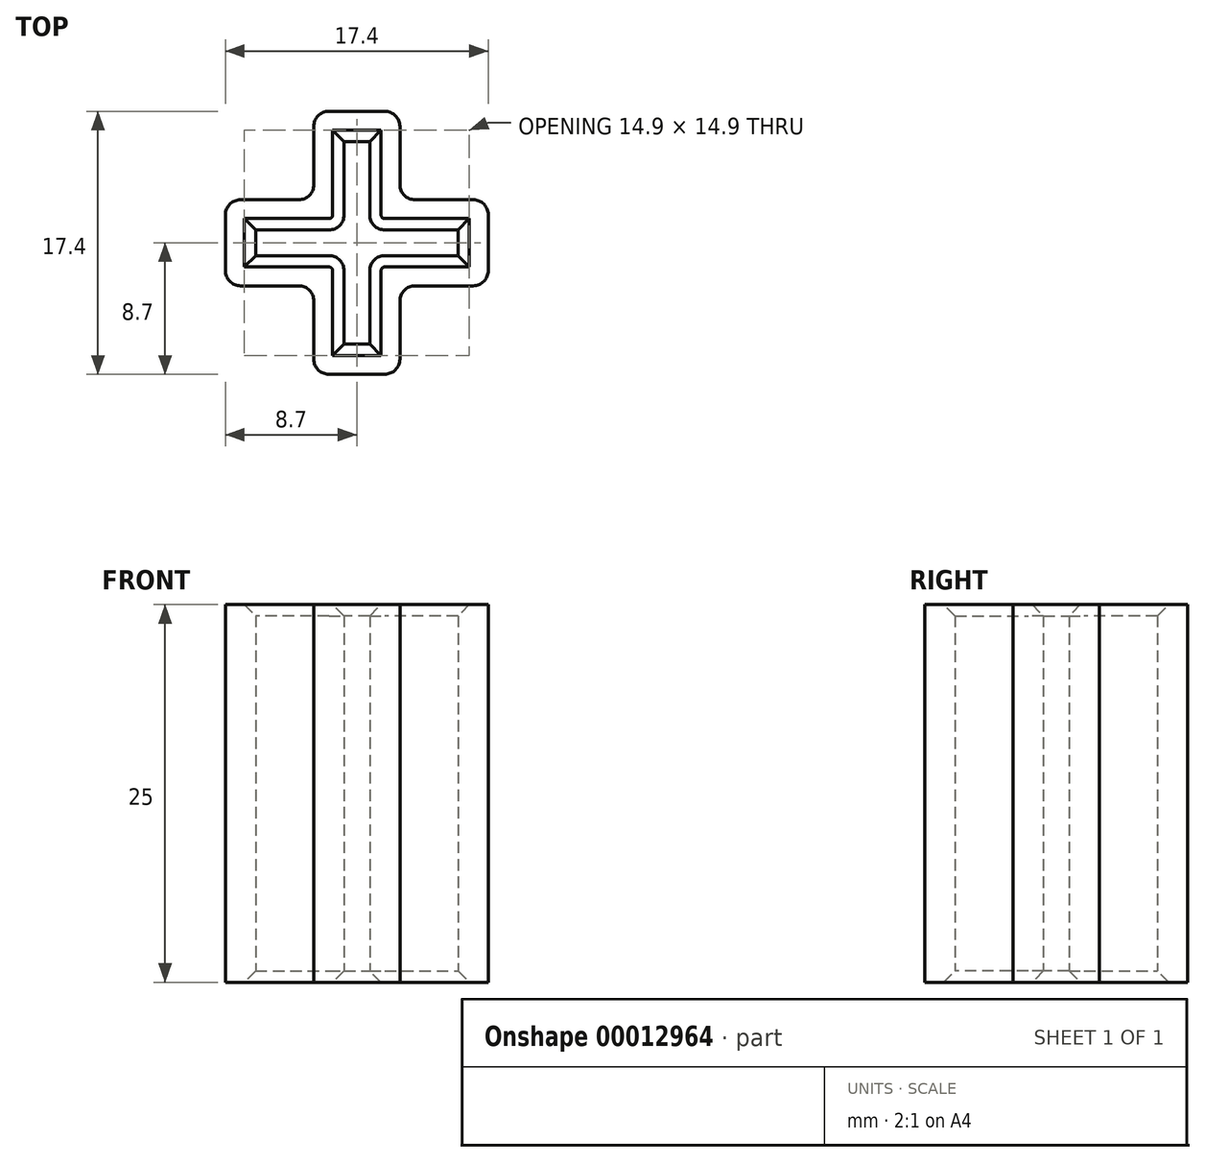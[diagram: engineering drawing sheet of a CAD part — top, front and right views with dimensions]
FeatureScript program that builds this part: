
annotation { "Feature Type Name" : "Feature", "Feature Type Description" : "" }
export const myFeature = defineFeature(function(context is Context, id is Id, definition is map)
    precondition{}
    {
        {
            var Q0;
            Q0=qCreatedBy(makeId("Top.planeOp"),FACE);
            var sketch = newSketch(context, id + "F0", { "sketchPlane" : qUnion([Q0])});
            skLineSegment(sketch, "E0.rect.bottom", {"start": v(-0.85, 6.7) * mm, "end": v(0.85, 6.7) * mm});
            skLineSegment(sketch, "E0.rect.top", {"start": v(-0.85, -6.7) * mm, "end": v(0.85, -6.7) * mm});
            skLineSegment(sketch, "E0.rect.left", {"start": v(-0.85, 6.7) * mm, "end": v(-0.85, -6.7) * mm});
            skLineSegment(sketch, "E0.rect.right", {"start": v(0.85, 6.7) * mm, "end": v(0.85, -6.7) * mm});
            skPoint(sketch, "E0.rect.middle", {"position": v(0, 0) * mm});
            skLineSegment(sketch, "E1.rect.bottom", {"start": v(-6.7, 0.85) * mm, "end": v(6.7, 0.85) * mm});
            skLineSegment(sketch, "E1.rect.top", {"start": v(-6.7, -0.85) * mm, "end": v(6.7, -0.85) * mm});
            skLineSegment(sketch, "E1.rect.left", {"start": v(-6.7, 0.85) * mm, "end": v(-6.7, -0.85) * mm});
            skLineSegment(sketch, "E1.rect.right", {"start": v(6.7, 0.85) * mm, "end": v(6.7, -0.85) * mm});
            skLineSegment(sketch, "E2.0", {"start": v(-8.7, 2.85) * mm, "end": v(8.7, 2.85) * mm});
            skLineSegment(sketch, "E2.1", {"start": v(-8.7, 2.85) * mm, "end": v(-8.7, -2.85) * mm});
            skLineSegment(sketch, "E2.2", {"start": v(-8.7, -2.85) * mm, "end": v(8.7, -2.85) * mm});
            skLineSegment(sketch, "E2.3", {"start": v(8.7, 2.85) * mm, "end": v(8.7, -2.85) * mm});
            skLineSegment(sketch, "E3.0", {"start": v(-2.85, 8.7) * mm, "end": v(-2.85, -8.7) * mm});
            skLineSegment(sketch, "E3.1", {"start": v(-2.85, 8.7) * mm, "end": v(2.85, 8.7) * mm});
            skLineSegment(sketch, "E3.2", {"start": v(2.85, 8.7) * mm, "end": v(2.85, -8.7) * mm});
            skLineSegment(sketch, "E3.3", {"start": v(-2.85, -8.7) * mm, "end": v(2.85, -8.7) * mm});
            skSolve(sketch);
        }
        {
            var Q0;
            {var subQ10=sQuery(id+"F0.wireOp",EDGE,"E1.rect.left");Q0=makeQuery(id+"F0.imprint","IMPRINT",FACE,{"disambiguationData":[TD([[makeQuery(id+"F0.imprint","IMPRINT",EDGE,{"derivedFrom":subQ10}),-1.0]])]});}
            var Q1;
            {var subQ1=sQuery(id+"F0.wireOp",EDGE,"E0.rect.left");var subQ5=sQuery(id+"F0.wireOp",EDGE,"E1.rect.top");var subQ7=makeQuery(id+"F0.imprint","INTERSECT",VERTEX,{"derivedFrom":[subQ1,subQ5]});Q1=makeQuery(id+"F0.imprint","IMPRINT",FACE,{"disambiguationData":[TD([[makeQuery(id+"F0.imprint","IMPRINT",EDGE,{"disambiguationData":[TD([[subQ7,-1.0]])],"derivedFrom":subQ1}),-1.0]])]});}
            var Q2;
            {var subQ10=sQuery(id+"F0.wireOp",EDGE,"E0.rect.top");Q2=makeQuery(id+"F0.imprint","IMPRINT",FACE,{"disambiguationData":[TD([[makeQuery(id+"F0.imprint","IMPRINT",EDGE,{"derivedFrom":subQ10}),-1.0]])]});}
            var Q3;
            {var subQ3=sQuery(id+"F0.wireOp",EDGE,"E2.0");var subQ5=sQuery(id+"F0.wireOp",EDGE,"E0.rect.left");var subQ6=makeQuery(id+"F0.imprint","INTERSECT",VERTEX,{"derivedFrom":[subQ5,subQ3]});Q3=makeQuery(id+"F0.imprint","IMPRINT",FACE,{"disambiguationData":[TD([[makeQuery(id+"F0.imprint","IMPRINT",EDGE,{"disambiguationData":[TD([[subQ6,-1.0]])],"derivedFrom":subQ5}),-1.0]])]});}
            var Q4;
            {var subQ10=sQuery(id+"F0.wireOp",EDGE,"E0.rect.bottom");Q4=makeQuery(id+"F0.imprint","IMPRINT",FACE,{"disambiguationData":[TD([[makeQuery(id+"F0.imprint","IMPRINT",EDGE,{"derivedFrom":subQ10}),1.0]])]});}
            var Q5;
            {var subQ3=sQuery(id+"F0.wireOp",EDGE,"E2.0");var subQ5=sQuery(id+"F0.wireOp",EDGE,"E0.rect.right");var subQ6=makeQuery(id+"F0.imprint","INTERSECT",VERTEX,{"derivedFrom":[subQ5,subQ3]});Q5=makeQuery(id+"F0.imprint","IMPRINT",FACE,{"disambiguationData":[TD([[makeQuery(id+"F0.imprint","IMPRINT",EDGE,{"disambiguationData":[TD([[subQ6,-1.0]])],"derivedFrom":subQ5}),1.0]])]});}
            var Q6;
            {var subQ1=sQuery(id+"F0.wireOp",EDGE,"E1.rect.top");var subQ5=sQuery(id+"F0.wireOp",EDGE,"E0.rect.right");var subQ7=makeQuery(id+"F0.imprint","INTERSECT",VERTEX,{"derivedFrom":[subQ5,subQ1]});Q6=makeQuery(id+"F0.imprint","IMPRINT",FACE,{"disambiguationData":[TD([[makeQuery(id+"F0.imprint","IMPRINT",EDGE,{"disambiguationData":[TD([[subQ7,-1.0]])],"derivedFrom":subQ5}),1.0]])]});}
            var Q7;
            {var subQ10=sQuery(id+"F0.wireOp",EDGE,"E1.rect.right");Q7=makeQuery(id+"F0.imprint","IMPRINT",FACE,{"disambiguationData":[TD([[makeQuery(id+"F0.imprint","IMPRINT",EDGE,{"derivedFrom":subQ10}),1.0]])]});}
            extrude(context, id + "F1", {"entities" : qUnion([Q0, Q1, Q2, Q3, Q4, Q5, Q6, Q7]), "endBound" : BoundingType.SYMMETRIC, "depth" : 25 * mm});
        }
        {
            var Q0;
            Q0=makeQuery(id+"F1.opExtrude","SWEPT_EDGE",EDGE,{"disambiguationData":[OSD([sQuery(id+"F0.wireOp",EDGE,"E0.rect.left"),sQuery(id+"F0.wireOp",EDGE,"E1.rect.top")])]});
            var Q1;
            Q1=makeQuery(id+"F1.opExtrude","SWEPT_EDGE",EDGE,{"disambiguationData":[OSD([sQuery(id+"F0.wireOp",EDGE,"E0.rect.right"),sQuery(id+"F0.wireOp",EDGE,"E1.rect.top")])]});
            var Q2;
            Q2=makeQuery(id+"F1.opExtrude","SWEPT_EDGE",EDGE,{"disambiguationData":[OSD([sQuery(id+"F0.wireOp",EDGE,"E0.rect.right"),sQuery(id+"F0.wireOp",EDGE,"E1.rect.bottom")])]});
            var Q3;
            Q3=makeQuery(id+"F1.opExtrude","SWEPT_EDGE",EDGE,{"disambiguationData":[OSD([sQuery(id+"F0.wireOp",EDGE,"E0.rect.left"),sQuery(id+"F0.wireOp",EDGE,"E1.rect.bottom")])]});
            fillet(context, id + "F2", {"entities" : qUnion([Q0, Q1, Q2, Q3]), "radius" : 1 * mm, "tangentPropagation" : true, "allowEdgeOverflow" : false});
        }
        {
            var Q0;
            Q0=makeQuery(id+"F1.opExtrude","SWEPT_EDGE",EDGE,{"disambiguationData":[OSD([sQuery(id+"F0.wireOp",EDGE,"E2.0"),sQuery(id+"F0.wireOp",EDGE,"E3.0")])]});
            var Q1;
            Q1=makeQuery(id+"F1.opExtrude","SWEPT_EDGE",EDGE,{"disambiguationData":[OSD([sQuery(id+"F0.wireOp",EDGE,"E2.0"),sQuery(id+"F0.wireOp",EDGE,"E2.1")])]});
            var Q2;
            Q2=makeQuery(id+"F1.opExtrude","SWEPT_EDGE",EDGE,{"disambiguationData":[OSD([sQuery(id+"F0.wireOp",EDGE,"E2.1"),sQuery(id+"F0.wireOp",EDGE,"E2.2")])]});
            var Q3;
            Q3=makeQuery(id+"F1.opExtrude","SWEPT_EDGE",EDGE,{"disambiguationData":[OSD([sQuery(id+"F0.wireOp",EDGE,"E3.0"),sQuery(id+"F0.wireOp",EDGE,"E3.1")])]});
            var Q4;
            Q4=makeQuery(id+"F1.opExtrude","SWEPT_EDGE",EDGE,{"disambiguationData":[OSD([sQuery(id+"F0.wireOp",EDGE,"E3.1"),sQuery(id+"F0.wireOp",EDGE,"E3.2")])]});
            var Q5;
            Q5=makeQuery(id+"F1.opExtrude","SWEPT_EDGE",EDGE,{"disambiguationData":[OSD([sQuery(id+"F0.wireOp",EDGE,"E2.0"),sQuery(id+"F0.wireOp",EDGE,"E2.3")])]});
            var Q6;
            Q6=makeQuery(id+"F1.opExtrude","SWEPT_EDGE",EDGE,{"disambiguationData":[OSD([sQuery(id+"F0.wireOp",EDGE,"E3.0"),sQuery(id+"F0.wireOp",EDGE,"E3.3")])]});
            var Q7;
            Q7=makeQuery(id+"F1.opExtrude","SWEPT_EDGE",EDGE,{"disambiguationData":[OSD([sQuery(id+"F0.wireOp",EDGE,"E2.2"),sQuery(id+"F0.wireOp",EDGE,"E3.0")])]});
            var Q8;
            Q8=makeQuery(id+"F1.opExtrude","SWEPT_EDGE",EDGE,{"disambiguationData":[OSD([sQuery(id+"F0.wireOp",EDGE,"E3.2"),sQuery(id+"F0.wireOp",EDGE,"E3.3")])]});
            var Q9;
            Q9=makeQuery(id+"F1.opExtrude","SWEPT_EDGE",EDGE,{"disambiguationData":[OSD([sQuery(id+"F0.wireOp",EDGE,"E2.2"),sQuery(id+"F0.wireOp",EDGE,"E2.3")])]});
            var Q10;
            Q10=makeQuery(id+"F1.opExtrude","SWEPT_EDGE",EDGE,{"disambiguationData":[OSD([sQuery(id+"F0.wireOp",EDGE,"E2.2"),sQuery(id+"F0.wireOp",EDGE,"E3.2")])]});
            var Q11;
            Q11=makeQuery(id+"F1.opExtrude","SWEPT_EDGE",EDGE,{"disambiguationData":[OSD([sQuery(id+"F0.wireOp",EDGE,"E2.0"),sQuery(id+"F0.wireOp",EDGE,"E3.2")])]});
            fillet(context, id + "F3", {"entities" : qUnion([Q0, Q1, Q2, Q3, Q4, Q5, Q6, Q7, Q8, Q9, Q10, Q11]), "radius" : 1 * mm, "tangentPropagation" : true, "allowEdgeOverflow" : false});
        }
        {
            var Q0;
            {var subQ0=sQuery(id+"F0.wireOp",EDGE,"E1.rect.bottom");Q0=makeQuery(id+"F1.opExtrude","CAP_EDGE",EDGE,{"disambiguationData":[OSD([subQ0]),TDD([makeQuery(id+"F0.imprint","IMPRINT",EDGE,{"disambiguationData":[TD([[makeQuery(id+"F0.imprint","INTERSECT",VERTEX,{"derivedFrom":[subQ0,sQuery(id+"F0.wireOp",EDGE,"E1.rect.left")]}),-1.0]])],"derivedFrom":subQ0}),makeQuery(id+"F0.imprint","IMPRINT",EDGE,{"disambiguationData":[TD([[makeQuery(id+"F0.imprint","INTERSECT",VERTEX,{"derivedFrom":[sQuery(id+"F0.wireOp",EDGE,"E0.rect.left"),subQ0]}),1.0]])],"derivedFrom":subQ0})])],"isStart":false});}
            var Q1;
            {var subQ0=sQuery(id+"F0.wireOp",EDGE,"E0.rect.right");var subQ1=makeQuery(id+"F0.imprint","INTERSECT",VERTEX,{"derivedFrom":[subQ0,sQuery(id+"F0.wireOp",EDGE,"E2.0")]});Q1=makeQuery(id+"F1.opExtrude","CAP_EDGE",EDGE,{"disambiguationData":[OSD([subQ0]),TDD([makeQuery(id+"F0.imprint","IMPRINT",EDGE,{"disambiguationData":[TD([[makeQuery(id+"F0.imprint","INTERSECT",VERTEX,{"derivedFrom":[sQuery(id+"F0.wireOp",EDGE,"E0.rect.bottom"),subQ0]}),-1.0]])],"derivedFrom":subQ0}),makeQuery(id+"F0.imprint","IMPRINT",EDGE,{"disambiguationData":[TD([[subQ1,-1.0]])],"derivedFrom":subQ0})])],"isStart":false});}
            var Q2;
            {var subQ0=sQuery(id+"F0.wireOp",EDGE,"E1.rect.top");Q2=makeQuery(id+"F1.opExtrude","CAP_EDGE",EDGE,{"disambiguationData":[OSD([subQ0]),TDD([makeQuery(id+"F0.imprint","IMPRINT",EDGE,{"disambiguationData":[TD([[makeQuery(id+"F0.imprint","INTERSECT",VERTEX,{"derivedFrom":[sQuery(id+"F0.wireOp",EDGE,"E0.rect.right"),subQ0]}),-1.0]])],"derivedFrom":subQ0}),makeQuery(id+"F0.imprint","IMPRINT",EDGE,{"disambiguationData":[TD([[makeQuery(id+"F0.imprint","INTERSECT",VERTEX,{"derivedFrom":[subQ0,sQuery(id+"F0.wireOp",EDGE,"E1.rect.right")]}),1.0]])],"derivedFrom":subQ0})])],"isStart":false});}
            var Q3;
            {var subQ0=sQuery(id+"F0.wireOp",EDGE,"E0.rect.left");Q3=makeQuery(id+"F1.opExtrude","CAP_EDGE",EDGE,{"disambiguationData":[OSD([subQ0]),TDD([makeQuery(id+"F0.imprint","IMPRINT",EDGE,{"disambiguationData":[TD([[makeQuery(id+"F0.imprint","INTERSECT",VERTEX,{"derivedFrom":[subQ0,sQuery(id+"F0.wireOp",EDGE,"E1.rect.top")]}),-1.0]])],"derivedFrom":subQ0}),makeQuery(id+"F0.imprint","IMPRINT",EDGE,{"disambiguationData":[TD([[makeQuery(id+"F0.imprint","INTERSECT",VERTEX,{"derivedFrom":[sQuery(id+"F0.wireOp",EDGE,"E0.rect.top"),subQ0]}),1.0]])],"derivedFrom":subQ0})])],"isStart":false});}
            var Q4;
            Q4=makeQuery(id+"F1.opExtrude","CAP_EDGE",EDGE,{"disambiguationData":[OSD([sQuery(id+"F0.wireOp",EDGE,"E1.rect.left")])],"isStart":false});
            var Q5;
            Q5=makeQuery(id+"F1.opExtrude","CAP_EDGE",EDGE,{"disambiguationData":[OSD([sQuery(id+"F0.wireOp",EDGE,"E0.rect.bottom")])],"isStart":false});
            var Q6;
            Q6=makeQuery(id+"F1.opExtrude","CAP_EDGE",EDGE,{"disambiguationData":[OSD([sQuery(id+"F0.wireOp",EDGE,"E1.rect.right")])],"isStart":false});
            var Q7;
            Q7=makeQuery(id+"F1.opExtrude","CAP_EDGE",EDGE,{"disambiguationData":[OSD([sQuery(id+"F0.wireOp",EDGE,"E0.rect.top")])],"isStart":false});
            var Q8;
            {var subQ0=sQuery(id+"F0.wireOp",EDGE,"E0.rect.right");Q8=makeQuery(id+"F1.opExtrude","CAP_EDGE",EDGE,{"disambiguationData":[OSD([subQ0]),TDD([makeQuery(id+"F0.imprint","IMPRINT",EDGE,{"disambiguationData":[TD([[makeQuery(id+"F0.imprint","INTERSECT",VERTEX,{"derivedFrom":[subQ0,sQuery(id+"F0.wireOp",EDGE,"E1.rect.top")]}),-1.0]])],"derivedFrom":subQ0}),makeQuery(id+"F0.imprint","IMPRINT",EDGE,{"disambiguationData":[TD([[makeQuery(id+"F0.imprint","INTERSECT",VERTEX,{"derivedFrom":[sQuery(id+"F0.wireOp",EDGE,"E0.rect.top"),subQ0]}),1.0]])],"derivedFrom":subQ0})])],"isStart":true});}
            var Q9;
            {var subQ0=sQuery(id+"F0.wireOp",EDGE,"E0.rect.left");Q9=makeQuery(id+"F1.opExtrude","CAP_EDGE",EDGE,{"disambiguationData":[OSD([subQ0]),TDD([makeQuery(id+"F0.imprint","IMPRINT",EDGE,{"disambiguationData":[TD([[makeQuery(id+"F0.imprint","INTERSECT",VERTEX,{"derivedFrom":[subQ0,sQuery(id+"F0.wireOp",EDGE,"E1.rect.top")]}),-1.0]])],"derivedFrom":subQ0}),makeQuery(id+"F0.imprint","IMPRINT",EDGE,{"disambiguationData":[TD([[makeQuery(id+"F0.imprint","INTERSECT",VERTEX,{"derivedFrom":[sQuery(id+"F0.wireOp",EDGE,"E0.rect.top"),subQ0]}),1.0]])],"derivedFrom":subQ0})])],"isStart":true});}
            var Q10;
            {var subQ0=sQuery(id+"F0.wireOp",EDGE,"E1.rect.bottom");Q10=makeQuery(id+"F1.opExtrude","CAP_EDGE",EDGE,{"disambiguationData":[OSD([subQ0]),TDD([makeQuery(id+"F0.imprint","IMPRINT",EDGE,{"disambiguationData":[TD([[makeQuery(id+"F0.imprint","INTERSECT",VERTEX,{"derivedFrom":[subQ0,sQuery(id+"F0.wireOp",EDGE,"E1.rect.left")]}),-1.0]])],"derivedFrom":subQ0}),makeQuery(id+"F0.imprint","IMPRINT",EDGE,{"disambiguationData":[TD([[makeQuery(id+"F0.imprint","INTERSECT",VERTEX,{"derivedFrom":[sQuery(id+"F0.wireOp",EDGE,"E0.rect.left"),subQ0]}),1.0]])],"derivedFrom":subQ0})])],"isStart":true});}
            var Q11;
            {var subQ0=sQuery(id+"F0.wireOp",EDGE,"E0.rect.right");var subQ1=makeQuery(id+"F0.imprint","INTERSECT",VERTEX,{"derivedFrom":[subQ0,sQuery(id+"F0.wireOp",EDGE,"E2.0")]});Q11=makeQuery(id+"F1.opExtrude","CAP_EDGE",EDGE,{"disambiguationData":[OSD([subQ0]),TDD([makeQuery(id+"F0.imprint","IMPRINT",EDGE,{"disambiguationData":[TD([[makeQuery(id+"F0.imprint","INTERSECT",VERTEX,{"derivedFrom":[sQuery(id+"F0.wireOp",EDGE,"E0.rect.bottom"),subQ0]}),-1.0]])],"derivedFrom":subQ0}),makeQuery(id+"F0.imprint","IMPRINT",EDGE,{"disambiguationData":[TD([[subQ1,-1.0]])],"derivedFrom":subQ0})])],"isStart":true});}
            var Q12;
            Q12=makeQuery(id+"F1.opExtrude","CAP_EDGE",EDGE,{"disambiguationData":[OSD([sQuery(id+"F0.wireOp",EDGE,"E1.rect.right")])],"isStart":true});
            var Q13;
            Q13=makeQuery(id+"F1.opExtrude","CAP_EDGE",EDGE,{"disambiguationData":[OSD([sQuery(id+"F0.wireOp",EDGE,"E0.rect.top")])],"isStart":true});
            var Q14;
            Q14=makeQuery(id+"F1.opExtrude","CAP_EDGE",EDGE,{"disambiguationData":[OSD([sQuery(id+"F0.wireOp",EDGE,"E1.rect.left")])],"isStart":true});
            var Q15;
            Q15=makeQuery(id+"F1.opExtrude","CAP_EDGE",EDGE,{"disambiguationData":[OSD([sQuery(id+"F0.wireOp",EDGE,"E0.rect.bottom")])],"isStart":true});
            chamfer(context, id + "F4", {"entities" : qUnion([Q0, Q1, Q2, Q3, Q4, Q5, Q6, Q7, Q8, Q9, Q10, Q11, Q12, Q13, Q14, Q15]), "width" : .75 * mm, "tangentPropagation" : true});
        }
    });
